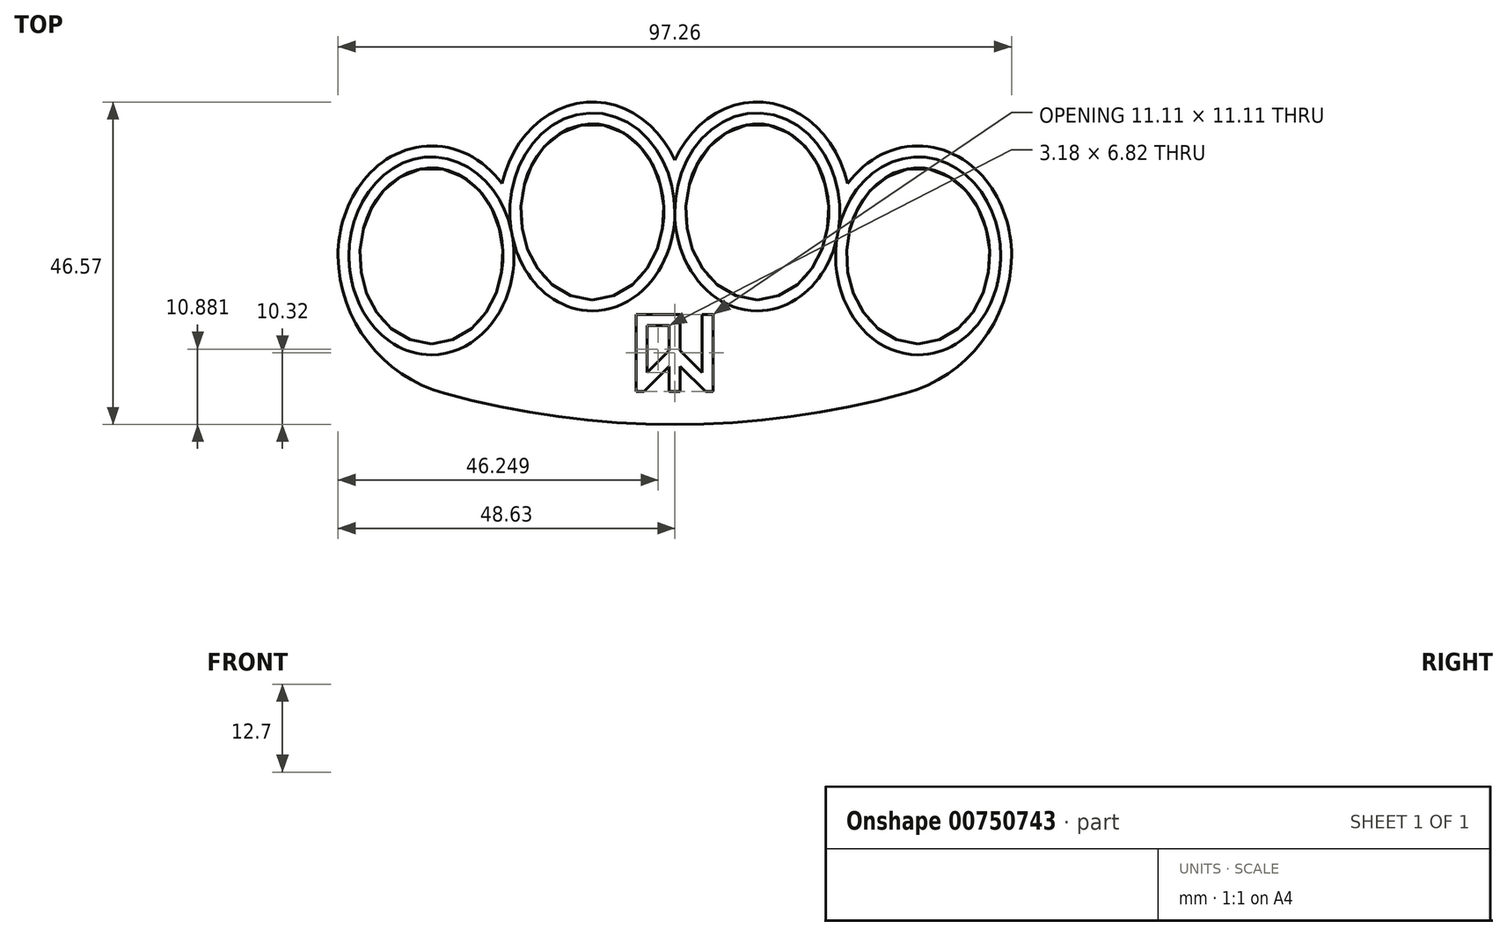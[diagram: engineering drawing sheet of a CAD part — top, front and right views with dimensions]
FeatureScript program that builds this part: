
annotation { "Feature Type Name" : "Feature", "Feature Type Description" : "" }
export const myFeature = defineFeature(function(context is Context, id is Id, definition is map)
    precondition{}
    {
        {
            var Q0;
            Q0=qCreatedBy(makeId("Top.planeOp"),FACE);
            var sketch = newSketch(context, id + "F0", { "sketchPlane" : qUnion([Q0])});
            skEllipse(sketch, "E0", {"center": v(-35.13, 25.4) * mm, "majorRadius": 12.7 * mm, "minorRadius": 10.33 * mm, "majorAxis": v(0, -1)});
            skEllipse(sketch, "E1", {"center": v(-11.91, 31.75) * mm, "majorRadius": 12.7 * mm, "minorRadius": 10.33 * mm, "majorAxis": v(0, -1)});
            skPoint(sketch, "E2", {"position": v(-11.91, 19.05) * mm});
            skPoint(sketch, "E3", {"position": v(-35.13, 12.7) * mm});
            skPoint(sketch, "E4", {"position": v(-27.13, 55.83) * mm});
            skPoint(sketch, "E5", {"position": v(-30.05, 81.5) * mm});
            skLineSegment(sketch, "E6", {"start": v(-35.13, 25.4) * mm, "end": v(-11.91, 31.75) * mm, "construction": true});
            skPoint(sketch, "E7", {"position": v(-25.05, 28.16) * mm});
            skPoint(sketch, "E8", {"position": v(-22, 29) * mm});
            skPoint(sketch, "E9", {"position": v(-1.59, 31.75) * mm});
            skLineSegment(sketch, "E10", {"start": v(0, -88.05) * mm, "end": v(0, 101.36) * mm, "construction": true});
            skEllipse(sketch, "E11.MirrorC", {"center": v(11.91, 31.75) * mm, "majorRadius": 12.7 * mm, "minorRadius": 10.33 * mm, "majorAxis": v(0, -1)});
            skEllipse(sketch, "E12.MirrorC", {"center": v(35.13, 25.4) * mm, "majorRadius": 12.7 * mm, "minorRadius": 10.33 * mm, "majorAxis": v(0, -1)});
            skPoint(sketch, "E13.MirrorP", {"position": v(11.91, 19.05) * mm});
            skPoint(sketch, "E14.MirrorP", {"position": v(35.13, 12.7) * mm});
            skEllipticalArc(sketch, "E15", {});
            skEllipticalArc(sketch, "E16", {});
            skEllipticalArc(sketch, "E17.trimOffspring", {"construction": true});
            skEllipticalArc(sketch, "E18.trimOffspring", {});
            skEllipticalArc(sketch, "E19.trimOffspring", {});
            skPoint(sketch, "E20.orphan", {"position": v(48.63, -2.1) * mm});
            skPoint(sketch, "E21.center.orphan", {"position": v(0, -160.82) * mm});
            skPoint(sketch, "E22.end.orphan", {"position": v(-56.13, 47.32) * mm});
            skPoint(sketch, "E22.start.orphan", {"position": v(-48.63, 25.4) * mm});
            skArc(sketch, "E23", {"start": v(-33.3, 5.55) * mm, "mid": v(-16.8, 2.18) * mm, "end": v(0, 1.06) * mm});
            skArc(sketch, "E24", {"start": v(-48.63, 25.4) * mm, "mid": v(-44.28, 12.92) * mm, "end": v(-33.3, 5.55) * mm});
            skArc(sketch, "E25.MirrorCS", {"start": v(33.3, 5.55) * mm, "mid": v(16.8, 2.18) * mm, "end": v(0, 1.06) * mm});
            skArc(sketch, "E26.MirrorCS", {"start": v(48.63, 25.4) * mm, "mid": v(44.28, 12.92) * mm, "end": v(33.3, 5.55) * mm});
            skEllipticalArc(sketch, "E27.MirrorCS", {});
            skEllipticalArc(sketch, "E28.MirrorCS", {});
            const initialGuessF0  = {"E15": [-0.03513316343952463, 0.0254, 0, -1, 0.015875, 0.013500100000000001, 2.2879470782142763, 4.988995807985221], "E16": [-0.01191260000000001, 0.03175, 0, -1, 0.015875, 0.013500100000000001, 4.907659616028547, 4.956799831093046], "E17.trimOffspring": [-0.01191260000000001, 0.03175, 0, -1, 0.015875, 0.013500100000000001, 5.429539731804069, 1.0809566052294173], "E18.trimOffspring": [-0.03513316343952463, 0.0254, 0, -1, 0.015875, 0.013500100000000001, 1.766066962438755, 1.8152071775032532], "E19.trimOffspring": [-0.01191260000000001, 0.03175, 0, -1, 0.015875, 0.013500100000000001, 2.060636048360376, 4.452224069159641], "E27.MirrorCS": [0.03513316343952463, 0.0254, 0, -1, 0.015875, 0.013500100000000001, 1.2941894991943652, 3.99523822896531], "E28.MirrorCS": [0.01191260000000001, 0.03175, 0, -1, 0.015875, 0.013500100000000001, 1.8309612380199454, 4.22254925881921]};
            skSetInitialGuess(sketch, initialGuessF0);
            skSolve(sketch);
        }
        {
            var Q0;
            Q0=makeQuery(id+"F0.imprint","IMPRINT",FACE,{"disambiguationData":[TD([[makeQuery(id+"F0.imprint","IMPRINT",EDGE,{"derivedFrom":sQuery(id+"F0.wireOp",EDGE,"E11.MirrorC")}),-1.0]])]});
            extrude(context, id + "F1", {"entities" : qUnion([Q0]), "depth" : 12.7 * mm, "offsetDistance" : 25.4 * mm});
        }
        {
            var Q0;
            Q0=makeQuery(id+"F1.opExtrude","SWEPT_FACE",FACE,{"disambiguationData":[OSD([sQuery(id+"F0.wireOp",EDGE,"E0")])]});
            var Q1;
            Q1=makeQuery(id+"F1.opExtrude","SWEPT_FACE",FACE,{"disambiguationData":[OSD([sQuery(id+"F0.wireOp",EDGE,"E1")])]});
            var Q2;
            Q2=makeQuery(id+"F1.opExtrude","SWEPT_FACE",FACE,{"disambiguationData":[OSD([sQuery(id+"F0.wireOp",EDGE,"E11.MirrorC")])]});
            var Q3;
            Q3=makeQuery(id+"F1.opExtrude","SWEPT_FACE",FACE,{"disambiguationData":[OSD([sQuery(id+"F0.wireOp",EDGE,"E12.MirrorC")])]});
            var Q4;
            Q4=makeQuery(id+"F1.opExtrude","CAP_EDGE",EDGE,{"disambiguationData":[OSD([sQuery(id+"F0.wireOp",EDGE,"E23"),sQuery(id+"F0.wireOp",EDGE,"E25.MirrorCS")])],"isStart":false});
            var Q5;
            Q5=makeQuery(id+"F1.opExtrude","CAP_EDGE",EDGE,{"disambiguationData":[OSD([sQuery(id+"F0.wireOp",EDGE,"E23"),sQuery(id+"F0.wireOp",EDGE,"E25.MirrorCS")])],"isStart":true});
            fillet(context, id + "F2", {"entities" : qUnion([Q0, Q1, Q2, Q3, Q4, Q5]), "radius" : 1.59 * mm, "tangentPropagation" : true, "allowEdgeOverflow" : false});
        }
        {
            var Q0;
            Q0=qCreatedBy(makeId("Top.planeOp"),FACE);
            var sketch = newSketch(context, id + "F3", { "sketchPlane" : qUnion([Q0])});
            skLineSegment(sketch, "E29.bottom", {"start": v(6.35, 5.03) * mm, "end": v(-6.35, 5.03) * mm, "construction": true});
            skLineSegment(sketch, "E29.top", {"start": v(6.35, 17.73) * mm, "end": v(-6.35, 17.73) * mm, "construction": true});
            skLineSegment(sketch, "E29.left", {"start": v(6.35, 5.03) * mm, "end": v(6.35, 17.73) * mm, "construction": true});
            skLineSegment(sketch, "E29.right", {"start": v(-6.35, 5.03) * mm, "end": v(-6.35, 17.73) * mm, "construction": true});
            skPoint(sketch, "E29.middle", {"position": v(0, 11.38) * mm});
            skLineSegment(sketch, "E30.bottom", {"start": v(5.56, 5.82) * mm, "end": v(4.43, 5.82) * mm});
            skLineSegment(sketch, "E30.top", {"start": v(5.56, 16.94) * mm, "end": v(3.97, 16.94) * mm});
            skLineSegment(sketch, "E30.left", {"start": v(5.56, 5.82) * mm, "end": v(5.56, 16.94) * mm});
            skLineSegment(sketch, "E30.right", {"start": v(-5.56, 5.82) * mm, "end": v(-5.56, 16.94) * mm});
            skLineSegment(sketch, "E31", {"start": v(3.97, 16.94) * mm, "end": v(3.97, 8.53) * mm});
            skLineSegment(sketch, "E32", {"start": v(3.97, 8.53) * mm, "end": v(0.8, 11.7) * mm});
            skLineSegment(sketch, "E33", {"start": v(-0.8, 11.7) * mm, "end": v(-3.97, 8.53) * mm});
            skLineSegment(sketch, "E34", {"start": v(-3.97, 8.53) * mm, "end": v(-3.97, 15.35) * mm});
            skLineSegment(sketch, "E35", {"start": v(-3.97, 15.35) * mm, "end": v(-0.8, 15.35) * mm});
            skLineSegment(sketch, "E36", {"start": v(-0.8, 15.35) * mm, "end": v(-0.8, 11.7) * mm});
            skLineSegment(sketch, "E37", {"start": v(4.43, 5.82) * mm, "end": v(0.8, 9.46) * mm});
            skLineSegment(sketch, "E38", {"start": v(-0.8, 9.46) * mm, "end": v(-4.43, 5.82) * mm});
            skLineSegment(sketch, "E39", {"start": v(0.8, 16.94) * mm, "end": v(0.8, 11.7) * mm});
            skPoint(sketch, "E40.orphan", {"position": v(0, 16.94) * mm});
            skLineSegment(sketch, "E41.trimOffspring", {"start": v(-0.8, 9.46) * mm, "end": v(-0.8, 5.82) * mm});
            skPoint(sketch, "E42.orphan", {"position": v(0, 5.82) * mm});
            skLineSegment(sketch, "E43.trimOffspring", {"start": v(0.8, 9.46) * mm, "end": v(0.8, 5.82) * mm});
            skLineSegment(sketch, "E44.trimOffspring", {"start": v(0.8, 5.82) * mm, "end": v(-0.8, 5.82) * mm});
            skLineSegment(sketch, "E45.trimOffspring", {"start": v(-4.43, 5.82) * mm, "end": v(-5.56, 5.82) * mm});
            skLineSegment(sketch, "E46.trimOffspring", {"start": v(0.8, 16.94) * mm, "end": v(-5.56, 16.94) * mm});
            skSolve(sketch);
        }
        {
            var Q0;
            Q0 = qSketchRegion(id + "F3", true);
            extrude(context, id + "F4", {"entities" : qUnion([Q0]), "operationType" : NewBodyOperationType.REMOVE, "depth" : 12.7 * mm, "offsetDistance" : 25.4 * mm, "hasSecondDirection" : true, "secondDirectionOppositeDirection" : false, "secondDirectionDepth" : 11.1 * mm});
        }
        {
            var Q0;
            Q0 = qSketchRegion(id + "F3", true);
            extrude(context, id + "F5", {"entities" : qUnion([Q0]), "operationType" : NewBodyOperationType.REMOVE, "depth" : 1.59 * mm, "offsetDistance" : 25.4 * mm});
        }
    });
